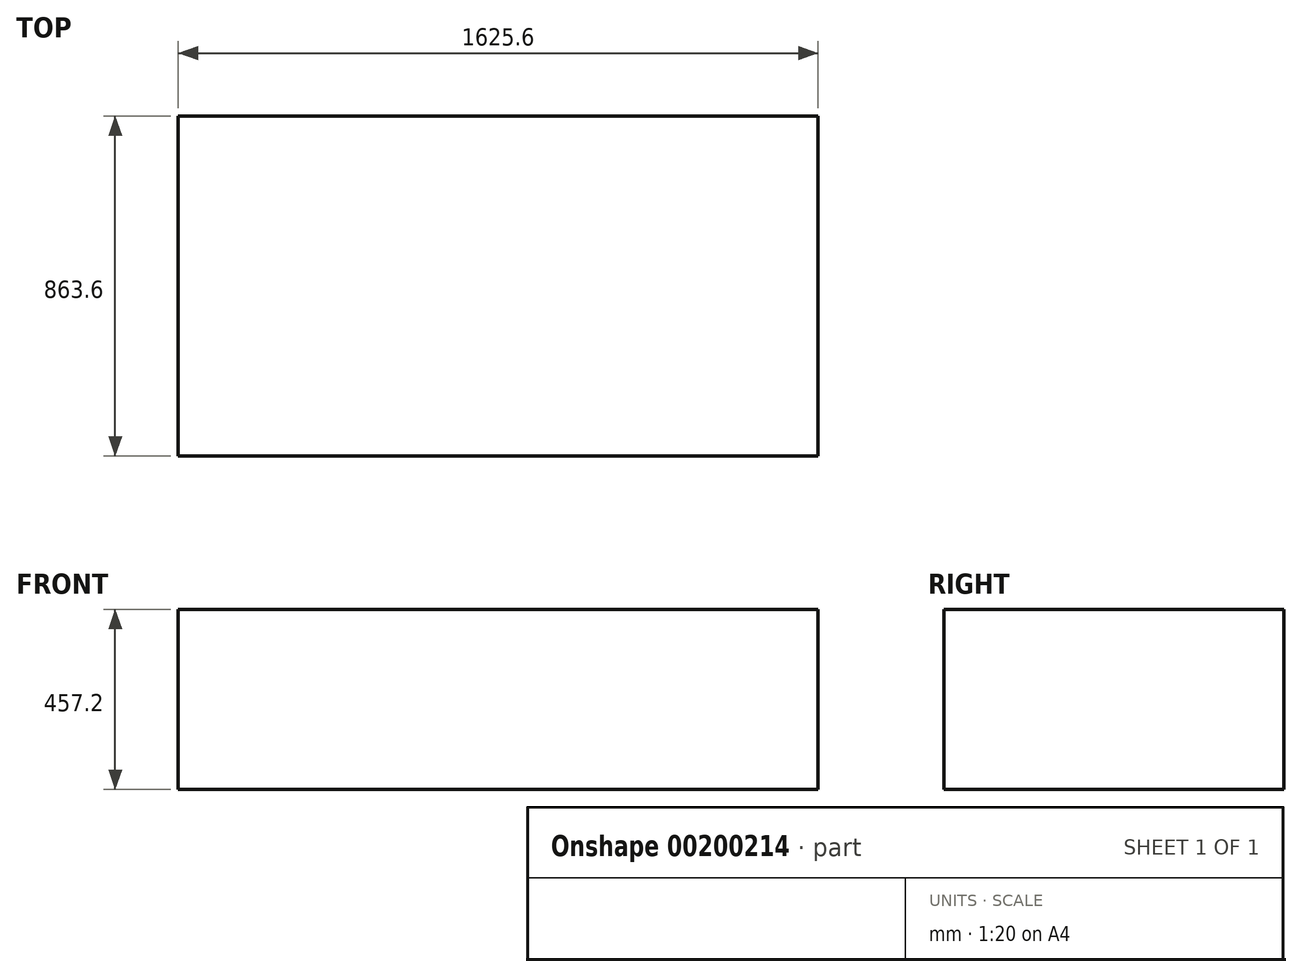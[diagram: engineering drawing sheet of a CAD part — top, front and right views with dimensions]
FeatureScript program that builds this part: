
annotation { "Feature Type Name" : "Feature", "Feature Type Description" : "" }
export const myFeature = defineFeature(function(context is Context, id is Id, definition is map)
    precondition{}
    {
        {
            var Q0;
            Q0=qCreatedBy(makeId("Front.planeOp"),FACE);
            var sketch = newSketch(context, id + "F0", { "sketchPlane" : qUnion([Q0])});
            skLineSegment(sketch, "E0.bottom", {"start": v(-834.2, 38.33) * mm, "end": v(791.4, 38.33) * mm});
            skLineSegment(sketch, "E0.top", {"start": v(-834.2, -418.87) * mm, "end": v(791.4, -418.87) * mm});
            skLineSegment(sketch, "E0.left", {"start": v(-834.2, 38.33) * mm, "end": v(-834.2, -418.87) * mm});
            skLineSegment(sketch, "E0.right", {"start": v(791.4, 38.33) * mm, "end": v(791.4, -418.87) * mm});
            skSolve(sketch);
        }
        {
            var Q0;
            Q0 = qSketchRegion(id + "F0", true);
            extrude(context, id + "F1", {"entities" : qUnion([Q0]), "depth" : 863.6 * mm});
        }
    });
